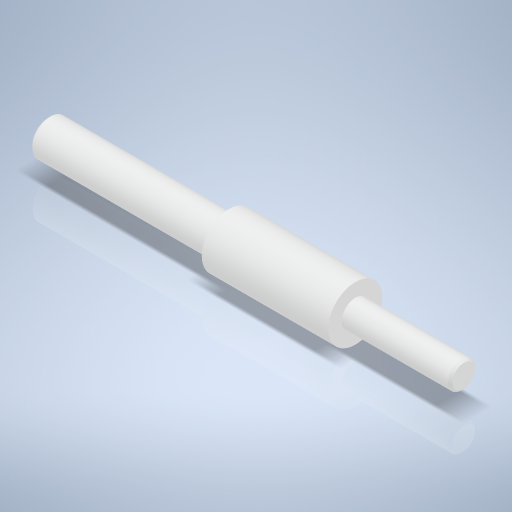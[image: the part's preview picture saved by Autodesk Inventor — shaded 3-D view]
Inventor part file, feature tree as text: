
AUTODESK INVENTOR PART (.ipt)
format: ipt  version: 2024 (Build 280153000, 153)  size: 271,360 bytes
history: native  units: mm
features: revolve x1, chamfer x1, sketch x1
ambient origin geometry x8: Origin, YZ Plane, XZ Plane, XY Plane, X Axis, Y Axis, Z Axis, Center Point
bodies: Volumenkörper1 (feature_tree)
feature tree (3):
  revolve  "Umdrehung1"
  chamfer  "Fasen1"  Distance=6.0mm
  sketch  "Skizze1"  dims[d0=28.0mm d2=6.0mm d3=8.0mm d4=24.0mm d5=40.0mm d6=12.0mm d7=90.0deg d8=0.5mm d9=2.0mm d10=45.0deg]
